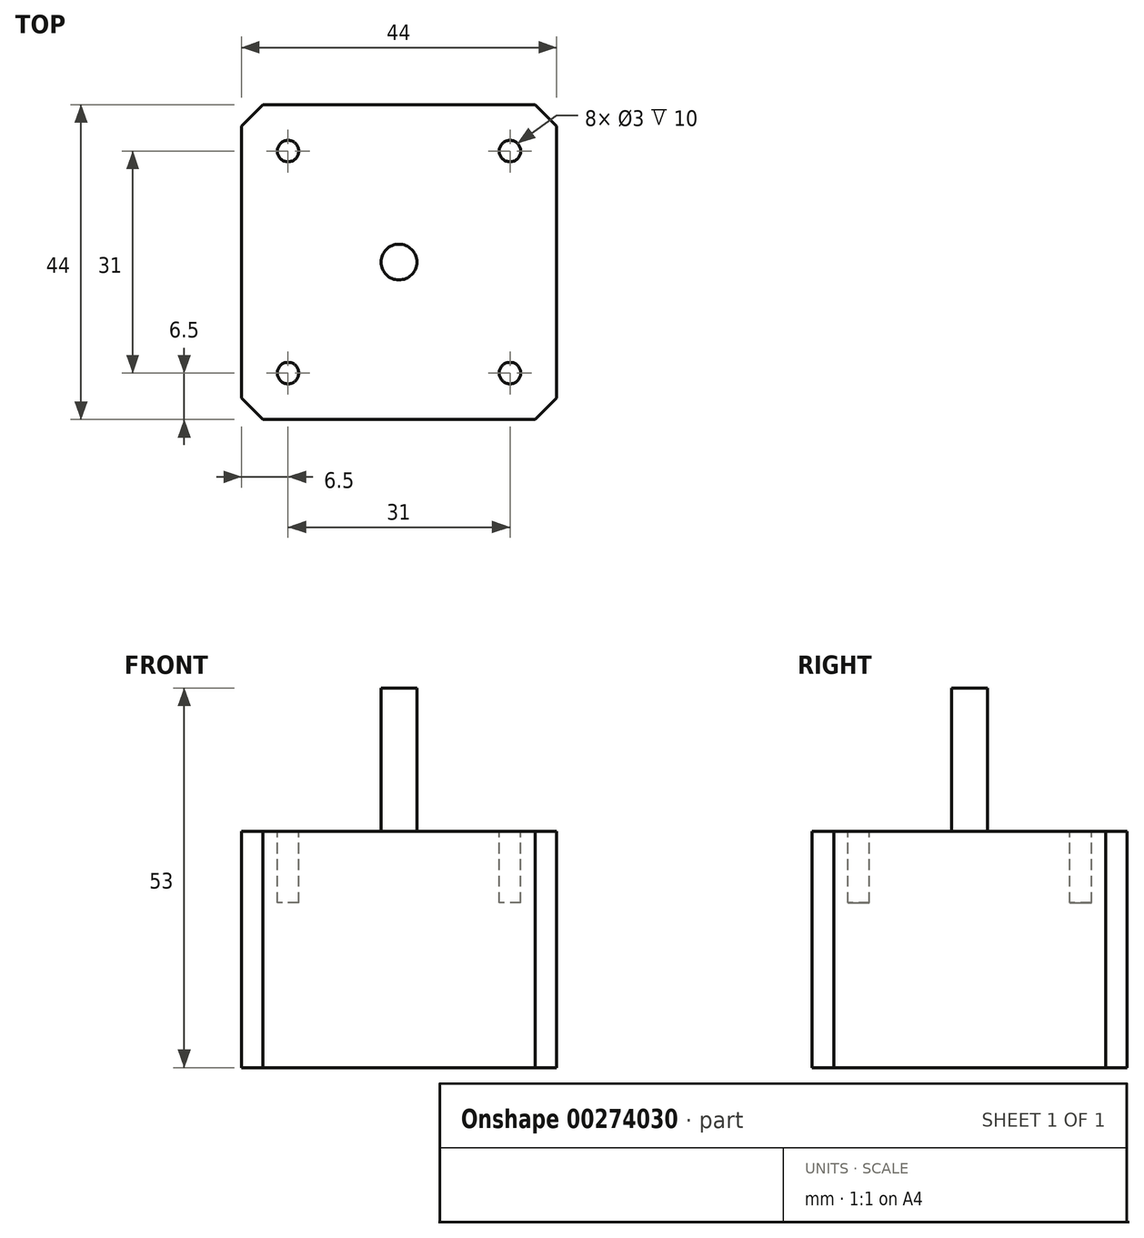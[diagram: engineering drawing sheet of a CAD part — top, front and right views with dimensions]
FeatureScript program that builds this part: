
annotation { "Feature Type Name" : "Feature", "Feature Type Description" : "" }
export const myFeature = defineFeature(function(context is Context, id is Id, definition is map)
    precondition{}
    {
        {
            var Q0;
            Q0=qCreatedBy(makeId("Top.planeOp"),FACE);
            var sketch = newSketch(context, id + "F0", { "sketchPlane" : qUnion([Q0])});
            skLineSegment(sketch, "E0.bottom", {"start": v(22, -22) * mm, "end": v(-22, -22) * mm});
            skLineSegment(sketch, "E0.top", {"start": v(22, 22) * mm, "end": v(-22, 22) * mm});
            skLineSegment(sketch, "E0.left", {"start": v(22, -22) * mm, "end": v(22, 22) * mm});
            skLineSegment(sketch, "E0.right", {"start": v(-22, -22) * mm, "end": v(-22, 22) * mm});
            skPoint(sketch, "E0.middle", {"position": v(0, 0) * mm});
            skCircle(sketch, "E1", {"center": v(0, 0) * mm, "radius": 2.5 * mm});
            skSolve(sketch);
        }
        {
            var Q0;
            Q0 = qSketchRegion(id + "F0", true);
            extrude(context, id + "F1", {"entities" : qUnion([Q0]), "depth" : 33 * mm});
        }
        {
            var Q0;
            Q0=makeQuery(id+"F0.imprint","IMPRINT",FACE,{"disambiguationData":[TD([[makeQuery(id+"F0.imprint","IMPRINT",EDGE,{"derivedFrom":sQuery(id+"F0.wireOp",EDGE,"E1")}),1.0]])]});
            extrude(context, id + "F2", {"entities" : qUnion([Q0]), "operationType" : NewBodyOperationType.ADD, "depth" : 53 * mm});
        }
        {
            var Q0;
            Q0=makeQuery(id+"F1.opExtrude","SWEPT_EDGE",EDGE,{"disambiguationData":[OSD([sQuery(id+"F0.wireOp",EDGE,"E0.top"),sQuery(id+"F0.wireOp",EDGE,"E0.left")])]});
            var Q1;
            Q1=makeQuery(id+"F1.opExtrude","SWEPT_EDGE",EDGE,{"disambiguationData":[OSD([sQuery(id+"F0.wireOp",EDGE,"E0.bottom"),sQuery(id+"F0.wireOp",EDGE,"E0.left")])]});
            var Q2;
            Q2=makeQuery(id+"F1.opExtrude","SWEPT_EDGE",EDGE,{"disambiguationData":[OSD([sQuery(id+"F0.wireOp",EDGE,"E0.top"),sQuery(id+"F0.wireOp",EDGE,"E0.right")])]});
            var Q3;
            Q3=makeQuery(id+"F1.opExtrude","SWEPT_EDGE",EDGE,{"disambiguationData":[OSD([sQuery(id+"F0.wireOp",EDGE,"E0.bottom"),sQuery(id+"F0.wireOp",EDGE,"E0.right")])]});
            chamfer(context, id + "F3", {"entities" : qUnion([Q0, Q1, Q2, Q3]), "width" : 3 * mm, "tangentPropagation" : true});
        }
        {
            var Q0;
            Q0=makeQuery(id+"F1.opExtrude","CAP_FACE",FACE,{"disambiguationData":[OSD([sQuery(id+"F0.wireOp",EDGE,"E0.bottom"),sQuery(id+"F0.wireOp",EDGE,"E0.top"),sQuery(id+"F0.wireOp",EDGE,"E0.left"),sQuery(id+"F0.wireOp",EDGE,"E0.right"),sQuery(id+"F0.wireOp",EDGE,"E1")])],"isStart":false});
            var sketch = newSketch(context, id + "F4", { "sketchPlane" : qUnion([Q0])});
            skCircle(sketch, "E2", {"center": v(-15.5, 15.5) * mm, "radius": 1.5 * mm});
            skCircle(sketch, "E3", {"center": v(15.5, 15.5) * mm, "radius": 1.5 * mm});
            skCircle(sketch, "E4", {"center": v(15.5, -15.5) * mm, "radius": 1.5 * mm});
            skCircle(sketch, "E5", {"center": v(-15.5, -15.5) * mm, "radius": 1.5 * mm});
            skSolve(sketch);
        }
        {
            var Q0;
            Q0 = qSketchRegion(id + "F4", true);
            extrude(context, id + "F5", {"entities" : qUnion([Q0]), "operationType" : NewBodyOperationType.REMOVE, "oppositeDirection" : true, "depth" : 10 * mm});
        }
        {
            var Q0;
            Q0=makeQuery(id+"F1.opExtrude","SWEPT_BODY",BODY,{"disambiguationData":[OSD([sQuery(id+"F0.wireOp",EDGE,"E0.bottom"),sQuery(id+"F0.wireOp",EDGE,"E0.top"),sQuery(id+"F0.wireOp",EDGE,"E0.left"),sQuery(id+"F0.wireOp",EDGE,"E0.right"),sQuery(id+"F0.wireOp",EDGE,"E1")])]});
            transform(context, id + "F6", {"entities" : qUnion([Q0]), "transformType" : TransformType.TRANSLATION_3D, "dx" : 0 * mm, "dy" : 0 * mm, "dz" : 0 * mm, "makeCopy" : true});
        }
    });
